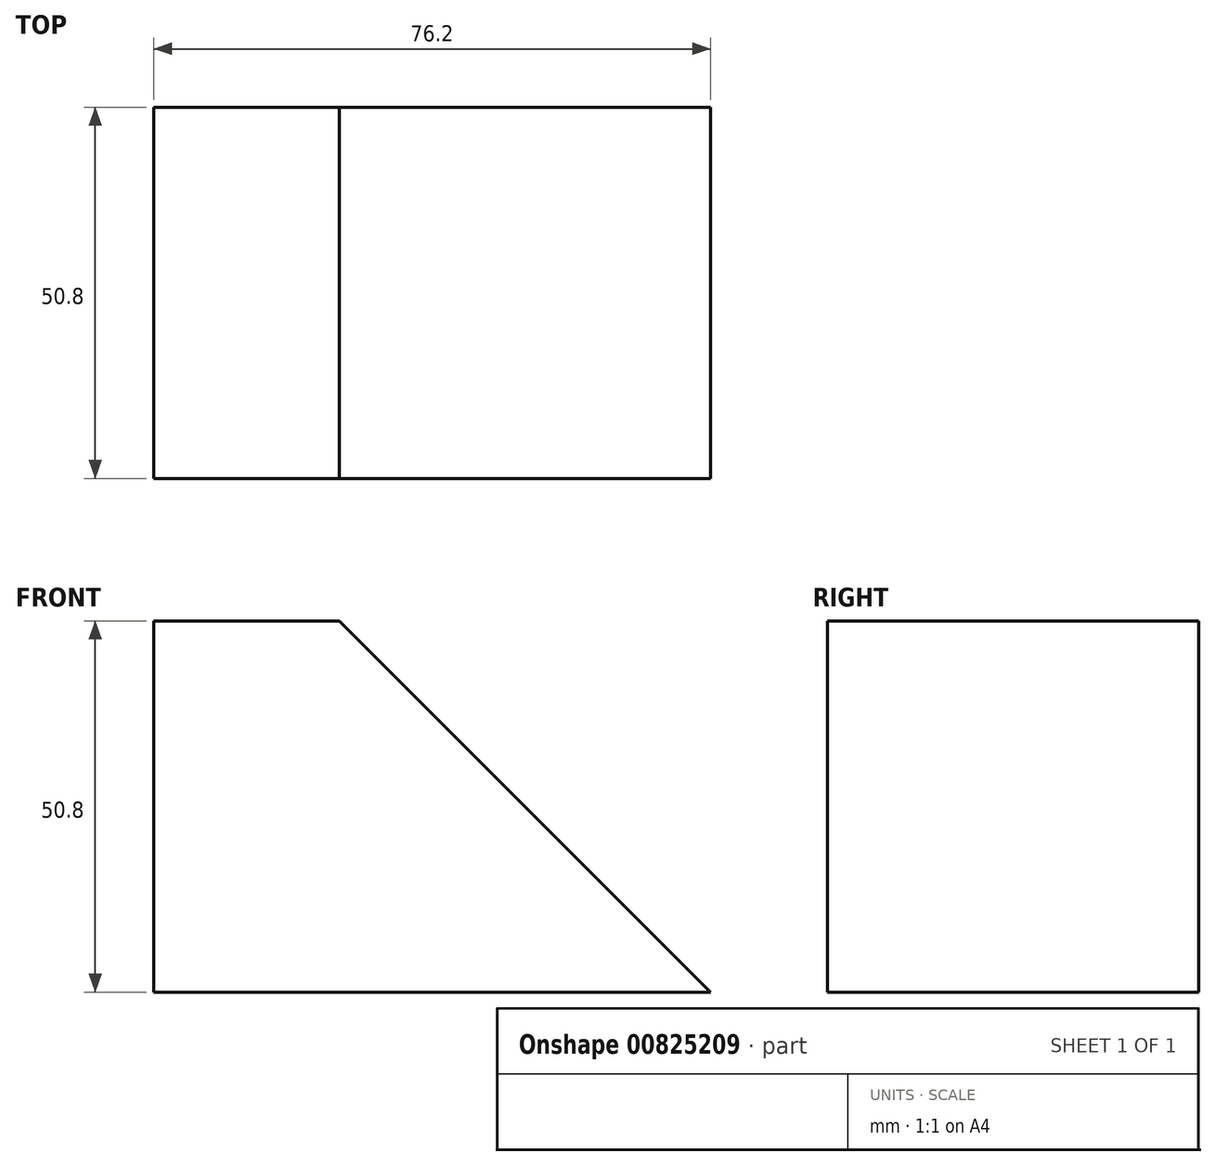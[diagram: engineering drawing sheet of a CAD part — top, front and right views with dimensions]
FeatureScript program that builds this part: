
annotation { "Feature Type Name" : "Feature", "Feature Type Description" : "" }
export const myFeature = defineFeature(function(context is Context, id is Id, definition is map)
    precondition{}
    {
        {
            var Q0;
            Q0=qCreatedBy(makeId("Front.planeOp"),FACE);
            var sketch = newSketch(context, id + "F0", { "sketchPlane" : qUnion([Q0])});
            skLineSegment(sketch, "E0", {"start": v(0, 0) * mm, "end": v(0, 50.8) * mm});
            skLineSegment(sketch, "E1", {"start": v(0, 50.8) * mm, "end": v(25.4, 50.8) * mm});
            skLineSegment(sketch, "E2", {"start": v(0, 0) * mm, "end": v(76.2, 0) * mm});
            skLineSegment(sketch, "E3", {"start": v(25.4, 50.8) * mm, "end": v(76.2, 0) * mm});
            skLineSegment(sketch, "E4", {"start": v(0, 0) * mm, "end": v(0, 25.4) * mm});
            skLineSegment(sketch, "E5", {"start": v(0, 25.4) * mm, "end": v(25.4, 25.4) * mm});
            skLineSegment(sketch, "E6", {"start": v(25.4, 25.4) * mm, "end": v(25.4, 50.8) * mm});
            skLineSegment(sketch, "E7", {"start": v(25.4, 25.4) * mm, "end": v(76.2, 0) * mm});
            skSolve(sketch);
        }
        {
            var Q0;
            Q0=makeQuery(id+"F0.imprint","IMPRINT",FACE,{"disambiguationData":[TD([[makeQuery(id+"F0.imprint","IMPRINT",EDGE,{"derivedFrom":sQuery(id+"F0.wireOp",EDGE,"E2")}),1.0]])]});
            var Q1;
            Q1=makeQuery(id+"F0.imprint","IMPRINT",FACE,{"disambiguationData":[TD([[makeQuery(id+"F0.imprint","IMPRINT",EDGE,{"derivedFrom":sQuery(id+"F0.wireOp",EDGE,"E3")}),-1.0]])]});
            var Q2;
            Q2=makeQuery(id+"F0.imprint","IMPRINT",FACE,{"disambiguationData":[TD([[makeQuery(id+"F0.imprint","IMPRINT",EDGE,{"derivedFrom":sQuery(id+"F0.wireOp",EDGE,"E0")}),-1.0]])]});
            extrude(context, id + "F1", {"entities" : qUnion([Q0, Q1, Q2]), "depth" : 50.8 * mm, "offsetDistance" : 25.4 * mm});
        }
    });
